# Revit family: Hager-Pablo-IP40-Transparent_Door-vuoto-IT-it
name_source: partatom
category: Electrical Equipment
units: mm (PartAtom-declared; Revit-internal decimal feet)

## family parameters
Cut with Voids When Loaded = No
Host = Face
Panel Configuration = Two Columns, Circuits Across
Part Type = Panelboard
Room Calculation Point = No
Round Connector Dimension = Use Diameter
Shared = No

## types (28) — shared parameters
EF000118 - con piastra di montaggio = No
EF000339 - tipo di copertura = EV004216 - porta
EF001062 - esecuzione EMC = No
EF001596 - Attacco Lampada = EV000139 - plastica
EF005474 - grado di protezione (IP) = EV006415 - IP40
EF006244 - coperchio/porta trasparente = Yes
EF006306 - con serratura = No
EF009212 - esecuzione coperchio = EV000116 - chiuso
EF015776 - Morsettiera di terra = No
EF015777 - Morsettiera neutra = No
HG000002 - Con porta = Yes
HG000003 - Gamma = Pablo
HG000005 - Spessore = 3 mm  [stored 0.00984252 ft]
HG000009 - Porta doppia a battente = No
HG000010 - Porte asimmetriche = No
HG000011 - File vuote nella parte basse = No
HG000017 - Distanza tra i poli = 18 mm  [stored 0.0590551 ft]
Manufacturer = Hager
Type Comments = Pablo
zero-valued in all types: Default Elevation, HG000001 - Numero di colonne, HG000007 - Numero di colonne vuote, HG000008 - Numero di file vuote

## per-type parameters (varying)
| type | EF000003 - Tipo di montaggio | EF000007 - colore | EF000008 - Larghezza | EF000040 - Altezza | EF000049 - profondità | EF000116 - numero RAL | EF000218 - profondità di incasso | EF000266 - numero di file | EF000332 - Altezza della parte incassata | EF000846 - larghezza di montaggio | EF001088 - possibilità di applicazione | EF001131 - profondità interna | EF001134 - barra DIN | EF002950 - Numero moduli DIN | EF004462 - tipo di chiusura | EF015941 - Segnale di passaggio porta | HG000004 - Codice produttore | HG000006 - Ad incasso | Model |
| A parete IP40 L175 A191 P25 4 Unità di divisione - B04951 | EV001247 - apparente/incassato | EV000154 - altri | 175 mm  [stored 0.574147 ft] | 191 mm  [stored 0.62664 ft] | 25 mm  [stored 0.082021 ft] | 7031 | 16 mm  [stored 0.0524934 ft] | 1 | 160 mm  [stored 0.524934 ft] | 175 mm  [stored 0.574147 ft] | Yes | 16 mm  [stored 0.0524934 ft] | Yes | 4 | EV001412 - cilindro | No | B04951 | No | B04951 |
| A parete IP40 L211 A191 P25 6 Unità di divisione - B04952 | EV001247 - apparente/incassato | EV000154 - altri | 211 mm  [stored 0.692257 ft] | 191 mm  [stored 0.62664 ft] | 25 mm  [stored 0.082021 ft] | 7031 | 16 mm  [stored 0.0524934 ft] | 1 | 160 mm  [stored 0.524934 ft] | 211 mm  [stored 0.692257 ft] | Yes | 16 mm  [stored 0.0524934 ft] | Yes | 6 | EV001412 - cilindro | No | B04952 | No | B04952 |
| A parete IP40 L280 A235 P25 8 Unità di divisione - B04953 | EV001247 - apparente/incassato | EV000154 - altri | 280 mm  [stored 0.918635 ft] | 235 mm  [stored 0.770997 ft] | 25 mm  [stored 0.082021 ft] | 7031 | 16 mm  [stored 0.0524934 ft] | 1 | 160 mm  [stored 0.524934 ft] | 280 mm  [stored 0.918635 ft] | Yes | 16 mm  [stored 0.0524934 ft] | Yes | 8 | EV001412 - cilindro | No | B04953 | No | B04953 |
| A parete IP40 L352 A275 P25 12 Unità di divisione - B04954 | EV001247 - apparente/incassato | EV000154 - altri | 352 mm  [stored 1.15486 ft] | 275 mm | 25 mm  [stored 0.082021 ft] | 7031 | 16 mm  [stored 0.0524934 ft] | 1 | 160 mm  [stored 0.524934 ft] | 352 mm  [stored 1.15486 ft] | Yes | 16 mm  [stored 0.0524934 ft] | Yes | 12 | EV001412 - cilindro | No | B04954 | No | B04954 |
| A parete IP40 L352 A425 P25 12 Unità di divisione - B04956 | EV001247 - apparente/incassato | EV000154 - altri | 352 mm  [stored 1.15486 ft] | 425 mm  [stored 1.39436 ft] | 25 mm  [stored 0.082021 ft] | 7031 | 16 mm  [stored 0.0524934 ft] | 2 | 405 mm | 352 mm  [stored 1.15486 ft] | Yes | 16 mm  [stored 0.0524934 ft] | Yes | 12 | EV001412 - cilindro | No | B04956 | No | B04956 |
| A parete IP40 L352 A575 P25 12 Unità di divisione - B04957 | EV001247 - apparente/incassato | EV000154 - altri | 352 mm  [stored 1.15486 ft] | 575 mm  [stored 1.88648 ft] | 25 mm  [stored 0.082021 ft] | 7031 | 16 mm  [stored 0.0524934 ft] | 3 | 405 mm | 352 mm  [stored 1.15486 ft] | Yes | 16 mm  [stored 0.0524934 ft] | Yes | 12 | EV001412 - cilindro | No | B04957 | No | B04957 |
| A parete IP40 L460 A275 P25 18 Unità di divisione - B04955 | EV001247 - apparente/incassato | EV000154 - altri | 460 mm  [stored 1.50919 ft] | 275 mm | 25 mm  [stored 0.082021 ft] | 7031 | 16 mm  [stored 0.0524934 ft] | 1 | 160 mm  [stored 0.524934 ft] | 460 mm  [stored 1.50919 ft] | Yes | 16 mm  [stored 0.0524934 ft] | Yes | 18 | EV001412 - cilindro | No | B04955 | No | B04955 |
| A parete IP40 L460 A575 P25 18 Unità di divisione - B04958 | EV001247 - apparente/incassato | EV000154 - altri | 460 mm  [stored 1.50919 ft] | 575 mm  [stored 1.88648 ft] | 25 mm  [stored 0.082021 ft] | 7031 | 16 mm  [stored 0.0524934 ft] | 3 | 405 mm | 460 mm  [stored 1.50919 ft] | Yes | 16 mm  [stored 0.0524934 ft] | Yes | 18 | EV001412 - cilindro | No | B04958 | No | B04958 |
| incassato IP40 L169 A180 P99 4 Unità di divisione - B04100 | EV000383 - incassato | EV000202 - bianco | 169 mm  [stored 0.554462 ft] | 180 mm  [stored 0.590551 ft] | 99 mm  [stored 0.324803 ft] | 9016 | 74 mm  [stored 0.242782 ft] | 1 | 160 mm  [stored 0.524934 ft] | 169 mm  [stored 0.554462 ft] | No | 99 mm  [stored 0.324803 ft] | Yes | 4 | EV000154 - altri | Yes | B04100 | Yes | B04100 |
| Incassato IP40 L175 A191 P25 4 Unità di divisione - B04951 | EV001247 - apparente/incassato | EV000154 - altri | 175 mm  [stored 0.574147 ft] | 191 mm  [stored 0.62664 ft] | 25 mm  [stored 0.082021 ft] | 7031 | 16 mm  [stored 0.0524934 ft] | 1 | 160 mm  [stored 0.524934 ft] | 175 mm  [stored 0.574147 ft] | Yes | 16 mm  [stored 0.0524934 ft] | Yes | 4 | EV001412 - cilindro | No | B04951 | Yes | B04951 |
| incassato IP40 L205 A180 P101 6 Unità di divisione - B04146 | EV000383 - incassato | EV000270 - grigio | 205 mm  [stored 0.672572 ft] | 180 mm  [stored 0.590551 ft] | 101 mm  [stored 0.331365 ft] | 9016 | 74 mm  [stored 0.242782 ft] | 1 | 160 mm  [stored 0.524934 ft] | 205 mm  [stored 0.672572 ft] | No | 101 mm  [stored 0.331365 ft] | Yes | 6 | EV000154 - altri | Yes | B04146 | Yes | B04146 |
| Incassato IP40 L211 A191 P25 6 Unità di divisione - B04952 | EV001247 - apparente/incassato | EV000154 - altri | 211 mm  [stored 0.692257 ft] | 191 mm  [stored 0.62664 ft] | 25 mm  [stored 0.082021 ft] | 7031 | 16 mm  [stored 0.0524934 ft] | 1 | 160 mm  [stored 0.524934 ft] | 211 mm  [stored 0.692257 ft] | Yes | 16 mm  [stored 0.0524934 ft] | Yes | 6 | EV001412 - cilindro | No | B04952 | Yes | B04952 |
| incassato IP40 L261 A225 P102 8 Unità di divisione - B04101 | EV000383 - incassato | EV000270 - grigio | 261 mm | 225 mm  [stored 0.738189 ft] | 102 mm | 9016 | 74 mm  [stored 0.242782 ft] | 1 | 160 mm  [stored 0.524934 ft] | 261 mm | No | 48 mm  [stored 0.15748 ft] | Yes | 8 | EV000154 - altri | Yes | B04101 | Yes | B04101 |
| incassato IP40 L261 A225 P102 8 Unità di divisione - B04108 | EV000383 - incassato | EV000270 - grigio | 261 mm | 225 mm  [stored 0.738189 ft] | 102 mm | 9016 | 74 mm  [stored 0.242782 ft] | 1 | 160 mm  [stored 0.524934 ft] | 261 mm | No | 102 mm | Yes | 8 | EV000154 - altri | Yes | B04108 | Yes | B04108 |
| Incassato IP40 L280 A235 P25 8 Unità di divisione - B04953 | EV001247 - apparente/incassato | EV000154 - altri | 280 mm  [stored 0.918635 ft] | 235 mm  [stored 0.770997 ft] | 25 mm  [stored 0.082021 ft] | 7031 | 16 mm  [stored 0.0524934 ft] | 1 | 160 mm  [stored 0.524934 ft] | 280 mm  [stored 0.918635 ft] | Yes | 16 mm  [stored 0.0524934 ft] | Yes | 8 | EV001412 - cilindro | No | B04953 | Yes | B04953 |
| incassato IP40 L333 A275 P108 12 Unità di divisione - B04102 | EV000383 - incassato | EV000270 - grigio | 333 mm  [stored 1.09252 ft] | 275 mm | 108 mm  [stored 0.354331 ft] | 9016 | 77 mm  [stored 0.252625 ft] | 1 | 160 mm  [stored 0.524934 ft] | 333 mm  [stored 1.09252 ft] | No | 108 mm  [stored 0.354331 ft] | Yes | 12 | EV000154 - altri | Yes | B04102 | Yes | B04102 |
| incassato IP40 L333 A275 P108 8 Unità di divisione - B04109 | EV000383 - incassato | EV000154 - altri | 333 mm  [stored 1.09252 ft] | 275 mm | 108 mm  [stored 0.354331 ft] | 9016 | 108 mm  [stored 0.354331 ft] | 1 | 160 mm  [stored 0.524934 ft] | 333 mm  [stored 1.09252 ft] | No | 108 mm  [stored 0.354331 ft] | No | 8 |  | Yes | B04109 | Yes | B04109 |
| incassato IP40 L345 A425 P109 12 Unità di divisione - B04104 | EV000383 - incassato | EV000270 - grigio | 345 mm  [stored 1.13189 ft] | 425 mm  [stored 1.39436 ft] | 109 mm  [stored 0.357612 ft] | 9016 | 77 mm  [stored 0.252625 ft] | 2 | 405 mm | 345 mm  [stored 1.13189 ft] | No | 109 mm  [stored 0.357612 ft] | Yes | 12 | EV000154 - altri | Yes | B04104 | Yes | B04104 |
| incassato IP40 L345 A425 P109 12 Unità di divisione - B04110 | EV000383 - incassato | EV000154 - altri | 345 mm  [stored 1.13189 ft] | 425 mm  [stored 1.39436 ft] | 109 mm  [stored 0.357612 ft] |  | 77 mm  [stored 0.252625 ft] | 2 | 405 mm | 345 mm  [stored 1.13189 ft] | Yes | 109 mm  [stored 0.357612 ft] | Yes | 12 | EV000154 - altri | Yes | B04110 | Yes | B04110 |
| Incassato IP40 L352 A275 P25 12 Unità di divisione - B04954 | EV001247 - apparente/incassato | EV000154 - altri | 352 mm  [stored 1.15486 ft] | 275 mm | 25 mm  [stored 0.082021 ft] | 7031 | 16 mm  [stored 0.0524934 ft] | 1 | 160 mm  [stored 0.524934 ft] | 352 mm  [stored 1.15486 ft] | Yes | 16 mm  [stored 0.0524934 ft] | Yes | 12 | EV001412 - cilindro | No | B04954 | Yes | B04954 |
| Incassato IP40 L352 A425 P25 12 Unità di divisione - B04956 | EV001247 - apparente/incassato | EV000154 - altri | 352 mm  [stored 1.15486 ft] | 425 mm  [stored 1.39436 ft] | 25 mm  [stored 0.082021 ft] | 7031 | 16 mm  [stored 0.0524934 ft] | 2 | 405 mm | 352 mm  [stored 1.15486 ft] | Yes | 16 mm  [stored 0.0524934 ft] | Yes | 12 | EV001412 - cilindro | No | B04956 | Yes | B04956 |
| Incassato IP40 L352 A575 P25 12 Unità di divisione - B04957 | EV001247 - apparente/incassato | EV000154 - altri | 352 mm  [stored 1.15486 ft] | 575 mm  [stored 1.88648 ft] | 25 mm  [stored 0.082021 ft] | 7031 | 16 mm  [stored 0.0524934 ft] | 3 | 405 mm | 352 mm  [stored 1.15486 ft] | Yes | 16 mm  [stored 0.0524934 ft] | Yes | 12 | EV001412 - cilindro | No | B04957 | Yes | B04957 |
| incassato IP40 L441 A300 P114 18 Unità di divisione - B04103 | EV000383 - incassato | EV000270 - grigio | 441 mm  [stored 1.44685 ft] | 300 mm | 114 mm  [stored 0.374016 ft] | 9016 | 77 mm  [stored 0.252625 ft] | 1 | 160 mm  [stored 0.524934 ft] | 441 mm  [stored 1.44685 ft] | No | 114 mm  [stored 0.374016 ft] | Yes | 18 | EV000154 - altri | Yes | B04103 | Yes | B04103 |
| incassato IP40 L455 A475 P114 12 Unità di divisione - B04105 | EV000383 - incassato | EV000270 - grigio | 455 mm | 475 mm  [stored 1.5584 ft] | 114 mm  [stored 0.374016 ft] | 9016 | 77 mm  [stored 0.252625 ft] | 2 | 405 mm | 455 mm | No | 114 mm  [stored 0.374016 ft] | Yes | 12 | EV000154 - altri | Yes | B04105 | Yes | B04105 |
| incassato IP40 L455 A650 P135 18 Unità di divisione - B04106 | EV000383 - incassato | EV000270 - grigio | 455 mm | 650 mm  [stored 2.13255 ft] | 135 mm  [stored 0.442913 ft] | 9016 | 77 mm  [stored 0.252625 ft] | 3 | 630 mm  [stored 2.06693 ft] | 455 mm | No | 135 mm  [stored 0.442913 ft] | Yes | 18 | EV000154 - altri | Yes | B04106 | Yes | B04106 |
| incassato IP40 L455 A850 P135 18 Unità di divisione - B04147 | EV000383 - incassato | EV000270 - grigio | 455 mm | 850 mm | 135 mm  [stored 0.442913 ft] | 9016 | 77 mm  [stored 0.252625 ft] | 4 | 821 mm | 455 mm | No | 135 mm  [stored 0.442913 ft] | Yes | 18 | EV000154 - altri | Yes | B04147 | Yes | B04147 |
| Incassato IP40 L460 A275 P25 18 Unità di divisione - B04955 | EV001247 - apparente/incassato | EV000154 - altri | 460 mm  [stored 1.50919 ft] | 275 mm | 25 mm  [stored 0.082021 ft] | 7031 | 16 mm  [stored 0.0524934 ft] | 1 | 160 mm  [stored 0.524934 ft] | 460 mm  [stored 1.50919 ft] | Yes | 16 mm  [stored 0.0524934 ft] | Yes | 18 | EV001412 - cilindro | No | B04955 | Yes | B04955 |
| Incassato IP40 L460 A575 P25 18 Unità di divisione - B04958 | EV001247 - apparente/incassato | EV000154 - altri | 460 mm  [stored 1.50919 ft] | 575 mm  [stored 1.88648 ft] | 25 mm  [stored 0.082021 ft] | 7031 | 16 mm  [stored 0.0524934 ft] | 3 | 405 mm | 460 mm  [stored 1.50919 ft] | Yes | 16 mm  [stored 0.0524934 ft] | Yes | 18 | EV001412 - cilindro | No | B04958 | Yes | B04958 |

note: [stored X ft] marks values corroborated as IEEE doubles in the binary element streams (Revit-internal decimal feet)

## geometry (parser evidence)
native form markers: Sweep x17
no freeform markers — native parametric forms only
